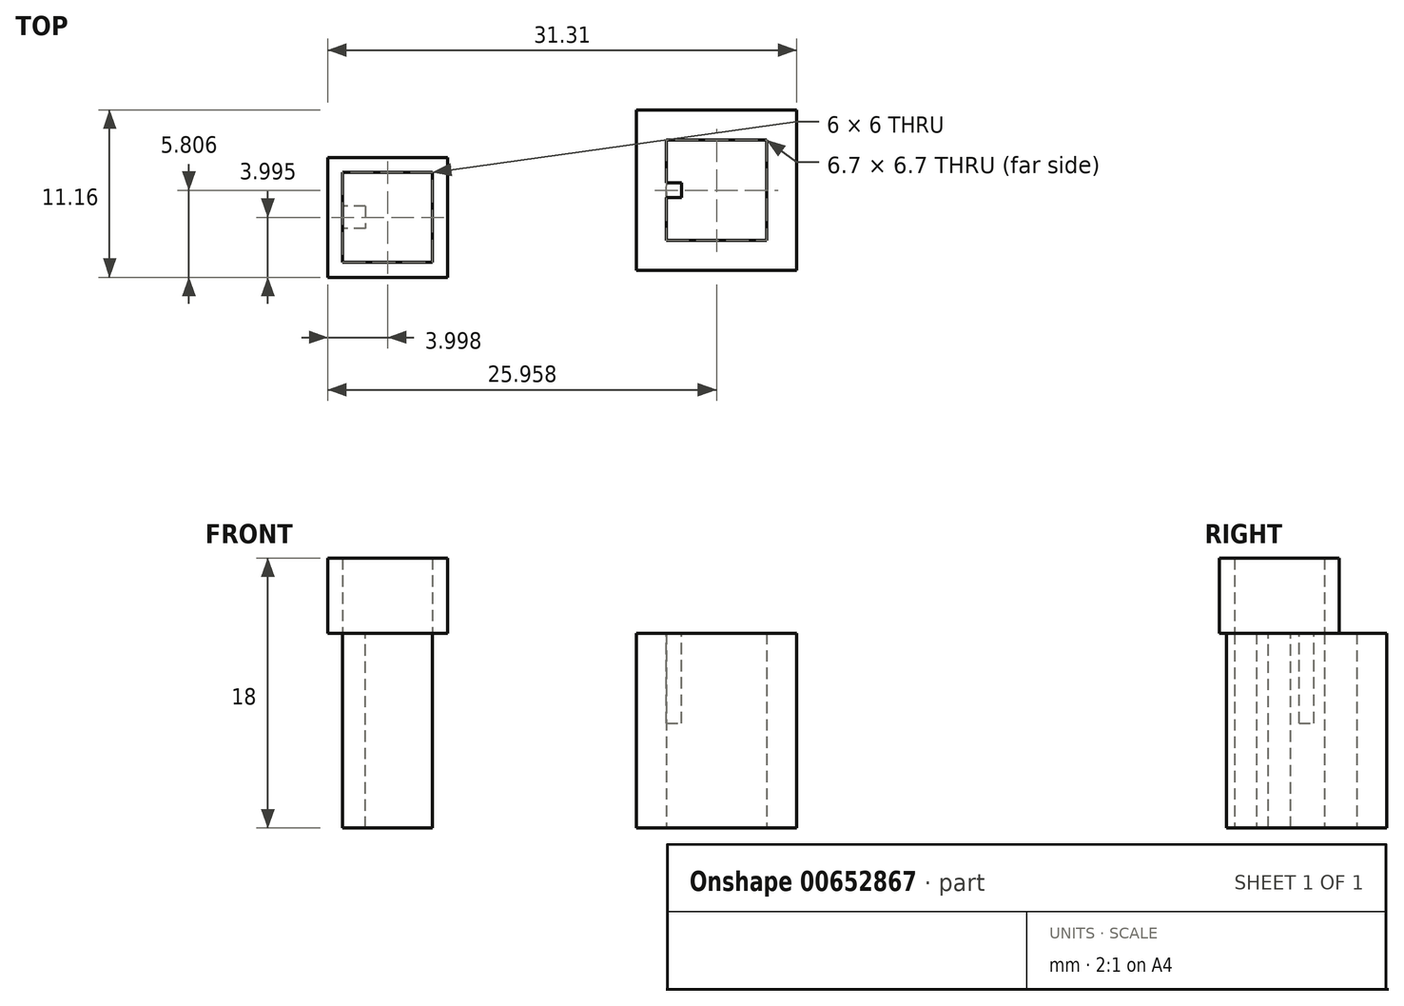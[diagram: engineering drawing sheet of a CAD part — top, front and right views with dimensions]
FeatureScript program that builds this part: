
annotation { "Feature Type Name" : "Feature", "Feature Type Description" : "" }
export const myFeature = defineFeature(function(context is Context, id is Id, definition is map)
    precondition{}
    {
        {
            var Q0;
            Q0=qCreatedBy(makeId("Top.planeOp"),FACE);
            var sketch = newSketch(context, id + "F0", { "sketchPlane" : qUnion([Q0])});
            skLineSegment(sketch, "E0.bottom", {"start": v(-11.97, 7.69) * mm, "end": v(-1.27, 7.69) * mm});
            skLineSegment(sketch, "E0.top", {"start": v(-11.97, -3.01) * mm, "end": v(-1.27, -3.01) * mm});
            skLineSegment(sketch, "E0.left", {"start": v(-11.97, 7.69) * mm, "end": v(-11.97, -3.01) * mm});
            skLineSegment(sketch, "E0.right", {"start": v(-1.27, 7.69) * mm, "end": v(-1.27, -3.01) * mm});
            skSolve(sketch);
        }
        {
            var Q0;
            Q0=makeQuery(id+"F0.imprint","IMPRINT",FACE,{"disambiguationData":[TD([[makeQuery(id+"F0.imprint","IMPRINT",EDGE,{"derivedFrom":sQuery(id+"F0.wireOp",EDGE,"E0.bottom")}),-1.0]])]});
            extrude(context, id + "F1", {"entities" : qUnion([Q0]), "depth" : 13 * mm, "offsetDistance" : 25 * mm});
        }
        {
            var Q0;
            Q0=makeQuery(id+"F1.opExtrude","CAP_FACE",FACE,{"disambiguationData":[OSD([sQuery(id+"F0.wireOp",EDGE,"E0.bottom"),sQuery(id+"F0.wireOp",EDGE,"E0.top"),sQuery(id+"F0.wireOp",EDGE,"E0.left"),sQuery(id+"F0.wireOp",EDGE,"E0.right")])],"isStart":false});
            shell(context, id + "F2", {"entities" : qUnion([Q0]), "thickness" : 2 * mm});
        }
        {
            var Q0;
            Q0=makeQuery(id+"F2.opShell","OFFSET_FACE",FACE,{"disambiguationData":[OSD([sQuery(id+"F0.wireOp",EDGE,"E0.bottom"),sQuery(id+"F0.wireOp",EDGE,"E0.top"),sQuery(id+"F0.wireOp",EDGE,"E0.left"),sQuery(id+"F0.wireOp",EDGE,"E0.right")])]});
            extrude(context, id + "F3", {"entities" : qUnion([Q0]), "operationType" : NewBodyOperationType.REMOVE, "oppositeDirection" : true, "depth" : 25 * mm, "offsetDistance" : 25 * mm});
        }
        {
            var Q0;
            Q0=qCreatedBy(makeId("Top.planeOp"),FACE);
            var sketch = newSketch(context, id + "F4", { "sketchPlane" : qUnion([Q0])});
            skLineSegment(sketch, "E1.bottom", {"start": v(-31.58, 3.53) * mm, "end": v(-25.58, 3.53) * mm});
            skLineSegment(sketch, "E1.top", {"start": v(-31.58, -2.47) * mm, "end": v(-25.58, -2.47) * mm});
            skLineSegment(sketch, "E1.left", {"start": v(-31.58, 3.53) * mm, "end": v(-31.58, -2.47) * mm});
            skLineSegment(sketch, "E1.right", {"start": v(-25.58, 3.53) * mm, "end": v(-25.58, -2.47) * mm});
            skSolve(sketch);
        }
        {
            var Q0;
            Q0 = qSketchRegion(id + "F4", true);
            extrude(context, id + "F5", {"entities" : qUnion([Q0]), "depth" : 13 * mm, "offsetDistance" : 25 * mm});
        }
        {
            var Q0;
            Q0=makeQuery(id+"F5.opExtrude","CAP_FACE",FACE,{"disambiguationData":[OSD([sQuery(id+"F4.wireOp",EDGE,"E1.bottom"),sQuery(id+"F4.wireOp",EDGE,"E1.top"),sQuery(id+"F4.wireOp",EDGE,"E1.left"),sQuery(id+"F4.wireOp",EDGE,"E1.right")])],"isStart":false});
            var sketch = newSketch(context, id + "F6", { "sketchPlane" : qUnion([Q0])});
            skLineSegment(sketch, "E2", {"start": v(-31.58, 3.53) * mm, "end": v(-25.58, -2.47) * mm});
            skLineSegment(sketch, "E3", {"start": v(-25.58, -2.47) * mm, "end": v(-25.58, 3.53) * mm});
            skLineSegment(sketch, "E4", {"start": v(-25.58, 3.53) * mm, "end": v(-31.58, -2.47) * mm});
            skPoint(sketch, "E5", {"position": v(-28.58, 0.53) * mm});
            skLineSegment(sketch, "E6.bottom", {"start": v(-24.58, -3.47) * mm, "end": v(-32.58, -3.47) * mm});
            skLineSegment(sketch, "E6.top", {"start": v(-24.58, 4.53) * mm, "end": v(-32.58, 4.53) * mm});
            skLineSegment(sketch, "E6.left", {"start": v(-24.58, -3.47) * mm, "end": v(-24.58, 4.53) * mm});
            skLineSegment(sketch, "E6.right", {"start": v(-32.58, -3.47) * mm, "end": v(-32.58, 4.53) * mm});
            skSolve(sketch);
        }
        {
            var Q0;
            Q0=makeQuery(id+"F6.imprint","IMPRINT",FACE,{"disambiguationData":[TD([[makeQuery(id+"F6.imprint","IMPRINT",EDGE,{"derivedFrom":sQuery(id+"F6.wireOp",EDGE,"E3")}),1.0]])]});
            extrude(context, id + "F7", {"entities" : qUnion([Q0]), "depth" : 5 * mm, "offsetDistance" : 25 * mm});
        }
        {
            var Q0;
            Q0=makeQuery(id+"F5.opExtrude","CAP_FACE",FACE,{"disambiguationData":[OSD([sQuery(id+"F4.wireOp",EDGE,"E1.bottom"),sQuery(id+"F4.wireOp",EDGE,"E1.top"),sQuery(id+"F4.wireOp",EDGE,"E1.left"),sQuery(id+"F4.wireOp",EDGE,"E1.right")])],"isStart":false});
            extrude(context, id + "F8", {"entities" : qUnion([Q0]), "depth" : 5 * mm, "offsetDistance" : 25 * mm});
        }
        {
            var Q0;
            {var subQ0=sQuery(id+"F0.wireOp",EDGE,"E0.left");Q0=makeQuery(id+"F3.boolean.opBoolean","MERGE",FACE,{"derivedFrom":[makeQuery(id+"F2.opShell","OFFSET_FACE",FACE,{"disambiguationData":[OSD([subQ0])]}),makeQuery(id+"F3.opExtrude","SWEPT_FACE",FACE,{"disambiguationData":[OSD([subQ0])]})]});}
            var sketch = newSketch(context, id + "F9", { "sketchPlane" : qUnion([Q0])});
            skPoint(sketch, "E7", {"position": v(2.34, 6.5) * mm});
            skLineSegment(sketch, "E8.bottom", {"start": v(1.84, 0) * mm, "end": v(2.84, 0) * mm});
            skLineSegment(sketch, "E8.top", {"start": v(1.84, 13) * mm, "end": v(2.84, 13) * mm});
            skLineSegment(sketch, "E8.left", {"start": v(1.84, 0) * mm, "end": v(1.84, 13) * mm});
            skLineSegment(sketch, "E8.right", {"start": v(2.84, 0) * mm, "end": v(2.84, 13) * mm});
            skPoint(sketch, "E9.orphan", {"position": v(-1.01, 13) * mm});
            skPoint(sketch, "E10.orphan", {"position": v(5.69, 0) * mm});
            skSolve(sketch);
        }
        {
            var Q0;
            Q0 = qSketchRegion(id + "F9", true);
            extrude(context, id + "F10", {"entities" : qUnion([Q0]), "operationType" : NewBodyOperationType.ADD, "depth" : 1 * mm, "offsetDistance" : 25 * mm});
        }
        {
            var Q0;
            Q0=makeQuery(id+"F10.opExtrude","CAP_FACE",FACE,{"disambiguationData":[OSD([sQuery(id+"F9.wireOp",EDGE,"E8.bottom"),sQuery(id+"F9.wireOp",EDGE,"E8.top"),sQuery(id+"F9.wireOp",EDGE,"E8.left"),sQuery(id+"F9.wireOp",EDGE,"E8.right")])],"isStart":false});
            var sketch = newSketch(context, id + "F11", { "sketchPlane" : qUnion([Q0])});
            skLineSegment(sketch, "E11", {"start": v(1.84, 0) * mm, "end": v(1.84, 7) * mm});
            skLineSegment(sketch, "E12", {"start": v(1.84, 7) * mm, "end": v(2.84, 7) * mm});
            skLineSegment(sketch, "E13", {"start": v(2.84, 7) * mm, "end": v(2.84, 0) * mm});
            skLineSegment(sketch, "E14", {"start": v(2.84, 0) * mm, "end": v(1.84, 0) * mm});
            skSolve(sketch);
        }
        {
            var Q0;
            Q0 = qSketchRegion(id + "F11", true);
            extrude(context, id + "F12", {"entities" : qUnion([Q0]), "operationType" : NewBodyOperationType.REMOVE, "oppositeDirection" : true, "depth" : 1 * mm, "offsetDistance" : 25 * mm});
        }
        {
            var Q0;
            Q0=makeQuery(id+"F5.opExtrude","SWEPT_FACE",FACE,{"disambiguationData":[OSD([sQuery(id+"F4.wireOp",EDGE,"E1.left")])]});
            var sketch = newSketch(context, id + "F13", { "sketchPlane" : qUnion([Q0])});
            skLineSegment(sketch, "E15", {"start": v(2.47, 0) * mm, "end": v(-3.53, 0) * mm});
            skPoint(sketch, "E16", {"position": v(-0.53, 6.5) * mm});
            skLineSegment(sketch, "E17.bottom", {"start": v(-1.28, 0) * mm, "end": v(0.22, 0) * mm});
            skLineSegment(sketch, "E17.top", {"start": v(-1.28, 13) * mm, "end": v(0.22, 13) * mm});
            skLineSegment(sketch, "E17.left", {"start": v(-1.28, 0) * mm, "end": v(-1.28, 13) * mm});
            skLineSegment(sketch, "E17.right", {"start": v(0.22, 0) * mm, "end": v(0.22, 13) * mm});
            skPoint(sketch, "E18.trimOffspring.end.orphan", {"position": v(2.47, 13) * mm});
            skSolve(sketch);
        }
        {
            var Q0;
            Q0 = qSketchRegion(id + "F13", true);
            extrude(context, id + "F14", {"entities" : qUnion([Q0]), "operationType" : NewBodyOperationType.REMOVE, "oppositeDirection" : true, "depth" : 1.5 * mm, "offsetDistance" : 25 * mm});
        }
    });
